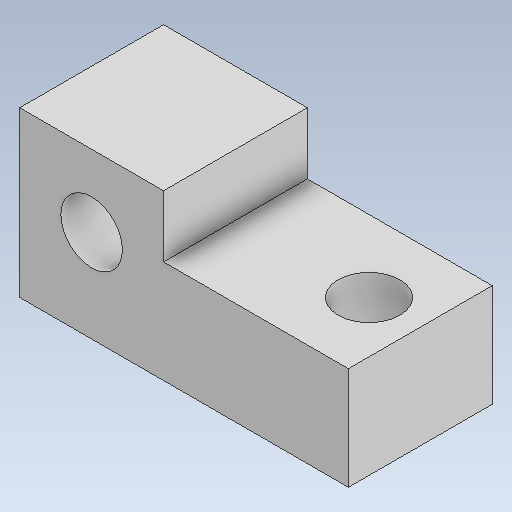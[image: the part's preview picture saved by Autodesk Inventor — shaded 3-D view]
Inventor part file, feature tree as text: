
AUTODESK INVENTOR PART (.ipt)
format: ipt  version: 2020 (Build 240168000, 168)  size: 135,168 bytes
history: native  units: mm
features: extrude x3, sketch x3, projected_geometry x2, other x1
ambient origin geometry x8: Origin, YZ Plane, XZ Plane, XY Plane, X Axis, Y Axis, Z Axis, Center Point
bodies: Body1 (feature_tree)
feature tree (9):
  other  "Твердое тело1"
  extrude  "Выдавливание1"  Depth=16.0mm
  extrude  "Выдавливание2"  Depth=7.0mm
  extrude  "Выдавливание3"  Depth=3.0mm
  sketch  "Эскиз1"
  sketch  "Эскиз2"
  projected_geometry  "Спроецированная петля1"
  sketch  "Эскиз3"
  projected_geometry  "Спроецированная петля2"
